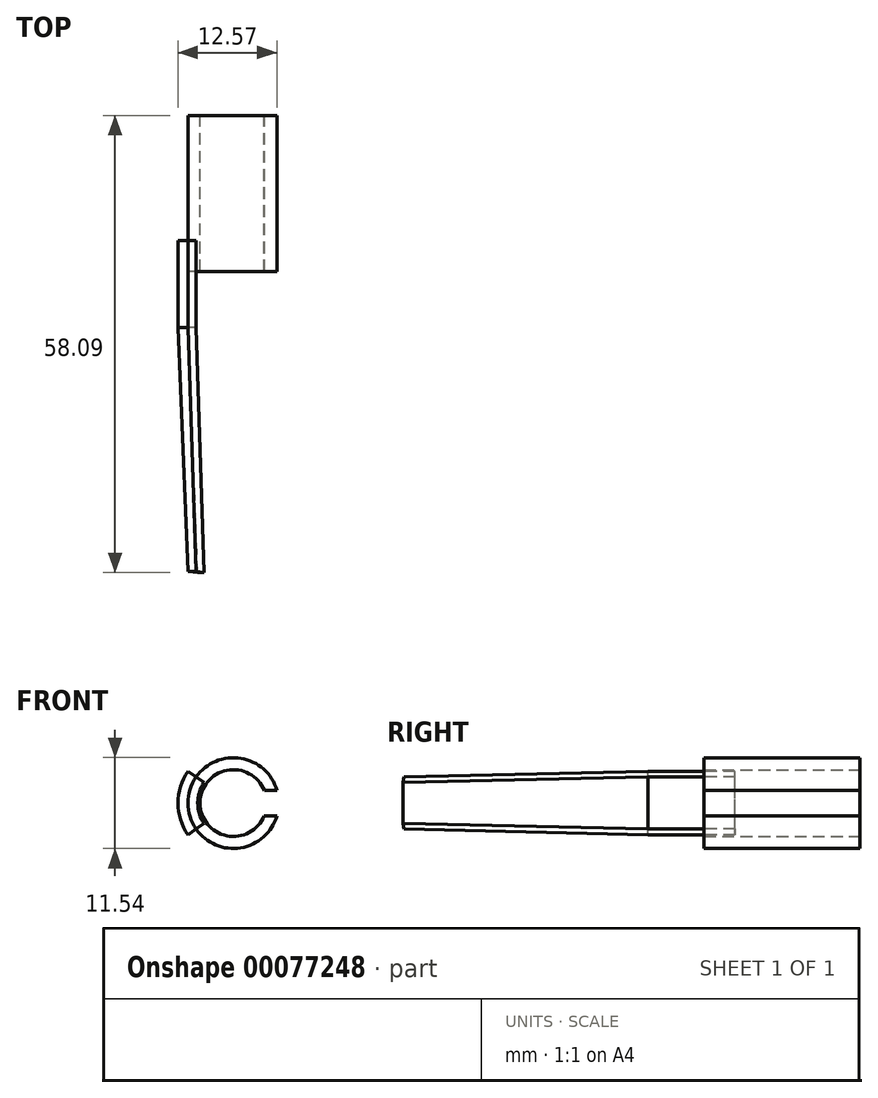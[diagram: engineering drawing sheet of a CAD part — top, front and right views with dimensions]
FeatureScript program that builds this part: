
annotation { "Feature Type Name" : "Feature", "Feature Type Description" : "" }
export const myFeature = defineFeature(function(context is Context, id is Id, definition is map)
    precondition{}
    {
        {
            var Q0;
            Q0=qCreatedBy(makeId("Top.planeOp"),FACE);
            var sketch = newSketch(context, id + "F0", { "sketchPlane" : qUnion([Q0])});
            skLineSegment(sketch, "E0.bottom", {"start": v(0, 0) * mm, "end": v(5.77, 0) * mm});
            skLineSegment(sketch, "E0.left", {"start": v(0, 0) * mm, "end": v(0, 19.82) * mm});
            skLineSegment(sketch, "E1", {"start": v(5.77, 31.37) * mm, "end": v(5.77, -8.6) * mm, "construction": true});
            skPoint(sketch, "E1.endSnap0", {"position": v(5.77, 0) * mm});
            skLineSegment(sketch, "E2", {"start": v(5.77, 19.82) * mm, "end": v(5.77, 0) * mm});
            skPoint(sketch, "E0.right.end.orphan", {"position": v(11.53, 19.82) * mm});
            skPoint(sketch, "E3.orphan", {"position": v(11.53, 0) * mm});
            skPoint(sketch, "E4.center.orphan", {"position": v(5.77, 19.82) * mm});
            skLineSegment(sketch, "E5", {"start": v(0, 19.82) * mm, "end": v(5.77, 19.82) * mm});
            skSolve(sketch);
        }
        {
            var Q0;
            Q0=makeQuery(id+"F0.imprint","IMPRINT",FACE,{"disambiguationData":[TD([[makeQuery(id+"F0.imprint","IMPRINT",EDGE,{"derivedFrom":sQuery(id+"F0.wireOp",EDGE,"E0.bottom")}),1.0]])]});
            var Q1;
            Q1=sQuery(id+"F0.wireOp",EDGE,"E2");
            revolve(context, id + "F1", {"entities" : qUnion([Q0]), "axis" : qUnion([Q1]), "revolveType" : RevolveType.FULL});
        }
        {
            var Q0;
            Q0=makeQuery(id+"F1.opRevolve","SWEPT_FACE",FACE,{"disambiguationData":[OSD([sQuery(id+"F0.wireOp",EDGE,"E5")])]});
            var sketch = newSketch(context, id + "F2", { "sketchPlane" : qUnion([Q0])});
            skCircle(sketch, "E6.0", {"center": v(-5.77, 0) * mm, "radius": 4.24 * mm});
            skCircle(sketch, "E7.0", {"center": v(-5.77, 0) * mm, "radius": 5.99 * mm});
            skSolve(sketch);
        }
        {
            var Q0;
            Q0=makeQuery(id+"F2.imprint","IMPRINT",FACE,{"disambiguationData":[TD([[makeQuery(id+"F2.imprint","IMPRINT",EDGE,{"derivedFrom":sQuery(id+"F2.wireOp",EDGE,"E6.0")}),1.0]])]});
            extrude(context, id + "F3", {"entities" : qUnion([Q0]), "operationType" : NewBodyOperationType.REMOVE, "endBound" : BoundingType.THROUGH_ALL, "oppositeDirection" : true, "depth" : 25.4 * mm});
        }
        {
            var Q0;
            Q0=qCreatedBy(makeId("Top.planeOp"),FACE);
            var sketch = newSketch(context, id + "F4", { "sketchPlane" : qUnion([Q0])});
            skLineSegment(sketch, "E8", {"start": v(0, 0) * mm, "end": v(0, 3.93) * mm});
            skLineSegment(sketch, "E9", {"start": v(0, 3.93) * mm, "end": v(-1.27, 3.93) * mm});
            skLineSegment(sketch, "E10", {"start": v(-1.27, 3.93) * mm, "end": v(-1.27, 0) * mm});
            skPoint(sketch, "E11.start.orphan", {"position": v(0, -38.1) * mm});
            skLineSegment(sketch, "E12", {"start": v(0, 0) * mm, "end": v(0, -7.15) * mm});
            skLineSegment(sketch, "E13", {"start": v(0, -7.15) * mm, "end": v(1.24, -38.27) * mm});
            skLineSegment(sketch, "E14", {"start": v(1.24, -38.27) * mm, "end": v(0, -38.1) * mm});
            skLineSegment(sketch, "E15", {"start": v(0, -38.1) * mm, "end": v(-1.27, -7.15) * mm});
            skLineSegment(sketch, "E16", {"start": v(-1.27, -7.15) * mm, "end": v(-1.27, 0) * mm});
            skSolve(sketch);
        }
        {
            var Q0;
            Q0=makeQuery(id+"F4.imprint","IMPRINT",FACE,{"disambiguationData":[TD([[makeQuery(id+"F4.imprint","IMPRINT",EDGE,{"derivedFrom":sQuery(id+"F4.wireOp",EDGE,"E8")}),1.0]])]});
            var Q1;
            {var subQ0=sQuery(id+"F4.wireOp",EDGE,"SNZlcRC2-aFMr-FLLu-pGcr-8FP9BlczLKat");Q1=makeQuery(id+"F4.imprint","IMPRINT",FACE,{"disambiguationData":[TD([[makeQuery(id+"F4.imprint","IMPRINT",EDGE,{"derivedFrom":subQ0}),1.0]])]});}
            var Q2;
            Q2=sQuery(id+"F0.wireOp",EDGE,"E1");
            revolve(context, id + "F5", {"operationType" : NewBodyOperationType.ADD, "entities" : qUnion([Q0, Q1]), "axis" : qUnion([Q2]), "revolveType" : RevolveType.TWO_DIRECTIONS, "angle" : 35 * degree, "angleBack" : 325 * degree});
        }
        {
            var Q0;
            Q0=qCreatedBy(makeId("Right.planeOp"),FACE);
            cPlane(context, id + "F6", {"entities" : qUnion([Q0]), "cplaneType" : CPlaneType.OFFSET, "offset" : 11.79 * mm, "width" : 152.4 * mm, "height" : 152.4 * mm});
        }
        {
            var Q0;
            Q0=qCreatedBy(id+"F6.planeOp",FACE);
            var sketch = newSketch(context, id + "F7", { "sketchPlane" : qUnion([Q0])});
            skLineSegment(sketch, "E17.bottom", {"start": v(19.84, 1.6) * mm, "end": v(0, 1.6) * mm});
            skLineSegment(sketch, "E17.top", {"start": v(19.84, -1.62) * mm, "end": v(0, -1.62) * mm});
            skLineSegment(sketch, "E17.left", {"start": v(19.84, 1.6) * mm, "end": v(19.84, -1.62) * mm});
            skLineSegment(sketch, "E17.right", {"start": v(0, 1.6) * mm, "end": v(0, -1.62) * mm});
            skSolve(sketch);
        }
        {
            var Q0;
            Q0=makeQuery(id+"F7.imprint","IMPRINT",FACE,{"disambiguationData":[TD([[makeQuery(id+"F7.imprint","IMPRINT",EDGE,{"derivedFrom":sQuery(id+"F7.wireOp",EDGE,"E17.bottom")}),1.0]])]});
            extrude(context, id + "F8", {"entities" : qUnion([Q0]), "operationType" : NewBodyOperationType.REMOVE, "oppositeDirection" : true, "depth" : 2.54 * mm});
        }
    });
